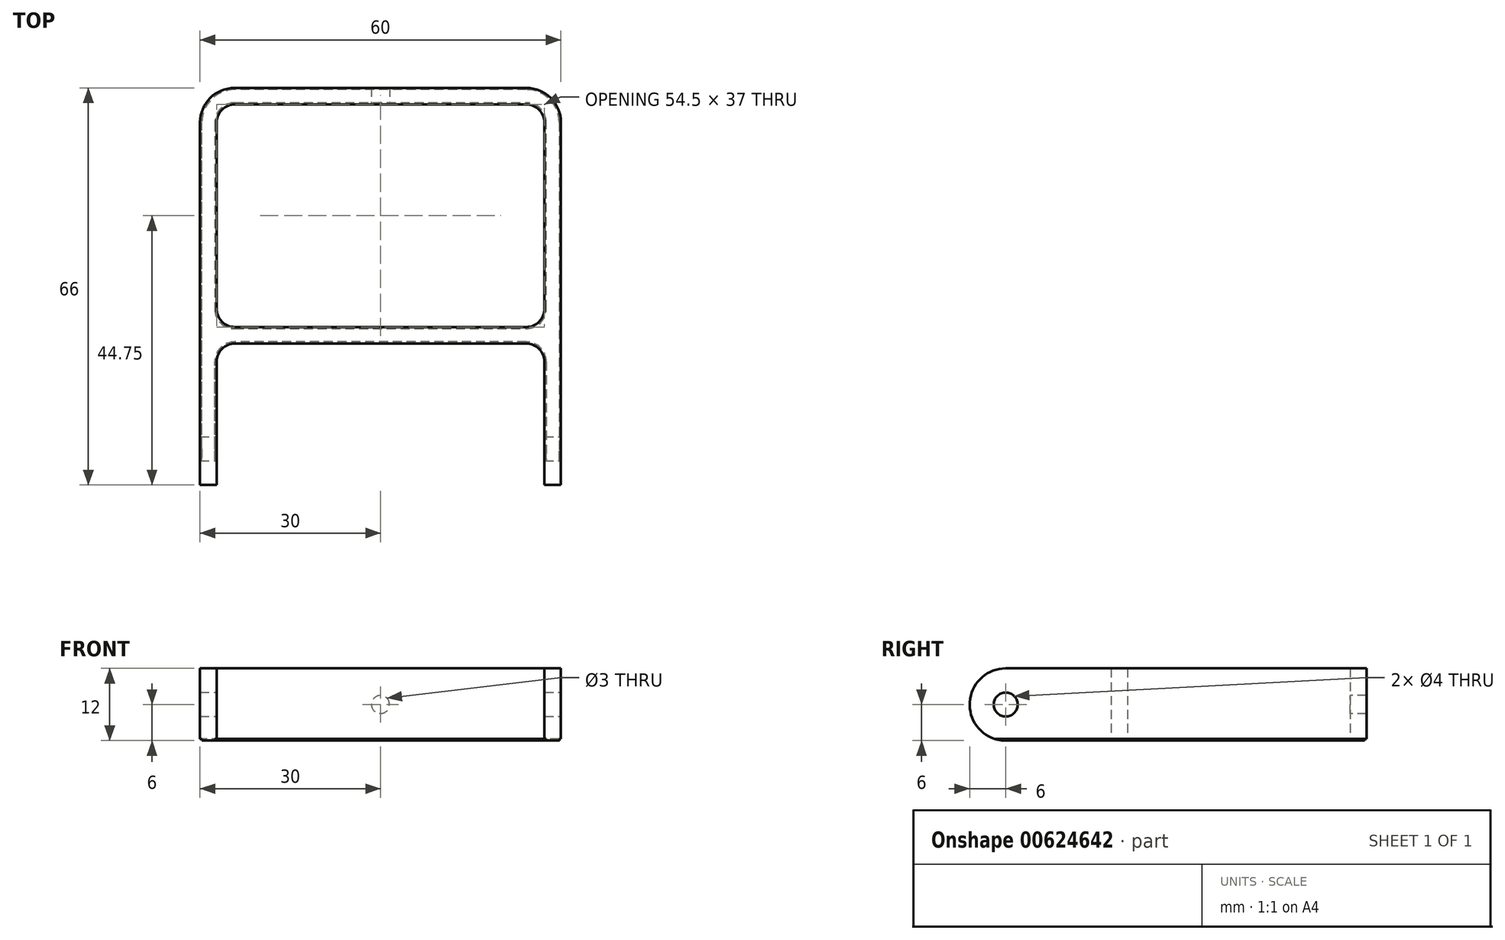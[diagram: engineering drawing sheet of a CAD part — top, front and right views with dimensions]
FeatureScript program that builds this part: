
annotation { "Feature Type Name" : "Feature", "Feature Type Description" : "" }
export const myFeature = defineFeature(function(context is Context, id is Id, definition is map)
    precondition{}
    {
        {
            var Q0;
            Q0=qCreatedBy(makeId("Top.planeOp"),FACE);
            var sketch = newSketch(context, id + "F0", { "sketchPlane" : qUnion([Q0])});
            skLineSegment(sketch, "E0", {"start": v(0, 0) * mm, "end": v(0, 63.25) * mm, "construction": true});
            skLineSegment(sketch, "E1", {"start": v(-27.25, 63.25) * mm, "end": v(27.25, 63.25) * mm});
            skLineSegment(sketch, "E2", {"start": v(27.25, 0) * mm, "end": v(30, 0) * mm});
            skLineSegment(sketch, "E3", {"start": v(30, 0) * mm, "end": v(30, 66) * mm});
            skLineSegment(sketch, "E4", {"start": v(30, 66) * mm, "end": v(-30, 66) * mm});
            skLineSegment(sketch, "E5", {"start": v(-30, 66) * mm, "end": v(-30, 0) * mm});
            skLineSegment(sketch, "E6", {"start": v(-30, 0) * mm, "end": v(-27.25, 0) * mm});
            skLineSegment(sketch, "E7", {"start": v(-27.25, 63.25) * mm, "end": v(-27.25, 26.25) * mm});
            skLineSegment(sketch, "E8", {"start": v(-27.25, 26.25) * mm, "end": v(27.25, 26.25) * mm});
            skLineSegment(sketch, "E9", {"start": v(27.25, 26.25) * mm, "end": v(27.25, 63.25) * mm});
            skLineSegment(sketch, "E10", {"start": v(27.25, 0) * mm, "end": v(27.25, 23.5) * mm});
            skLineSegment(sketch, "E11", {"start": v(27.25, 23.5) * mm, "end": v(-27.25, 23.5) * mm});
            skLineSegment(sketch, "E12", {"start": v(-27.25, 23.5) * mm, "end": v(-27.25, 0) * mm});
            skLineSegment(sketch, "E13", {"start": v(-27.25, 26.25) * mm, "end": v(-27.25, 23.5) * mm, "construction": true});
            skLineSegment(sketch, "E14", {"start": v(-27.25, 26.25) * mm, "end": v(-30, 26.25) * mm, "construction": true});
            skLineSegment(sketch, "E15", {"start": v(-27.25, 63.25) * mm, "end": v(-27.25, 66) * mm, "construction": true});
            skSolve(sketch);
        }
        {
            var Q0;
            Q0=qSketchRegion(id+"F0",true);
            extrude(context, id + "F1", {"entities" : qUnion([Q0]), "depth" : 12 * mm});
        }
        {
            var Q0;
            Q0=makeQuery(id+"F1.opExtrude","CAP_EDGE",EDGE,{"disambiguationData":[OSD([sQuery(id+"F0.wireOp",EDGE,"E6")])],"isStart":false});
            var Q1;
            Q1=makeQuery(id+"F1.opExtrude","CAP_EDGE",EDGE,{"disambiguationData":[OSD([sQuery(id+"F0.wireOp",EDGE,"E6")])],"isStart":true});
            var Q2;
            Q2=makeQuery(id+"F1.opExtrude","CAP_EDGE",EDGE,{"disambiguationData":[OSD([sQuery(id+"F0.wireOp",EDGE,"E2")])],"isStart":false});
            var Q3;
            Q3=makeQuery(id+"F1.opExtrude","CAP_EDGE",EDGE,{"disambiguationData":[OSD([sQuery(id+"F0.wireOp",EDGE,"E2")])],"isStart":true});
            fillet(context, id + "F2", {"entities" : qUnion([Q0, Q1, Q2, Q3]), "radius" : 6 * mm, "tangentPropagation" : true, "allowEdgeOverflow" : false});
        }
        {
            var Q0;
            Q0=makeQuery(id+"F1.opExtrude","SWEPT_FACE",FACE,{"disambiguationData":[OSD([sQuery(id+"F0.wireOp",EDGE,"E3")])]});
            var sketch = newSketch(context, id + "F3", { "sketchPlane" : qUnion([Q0])});
            skCircle(sketch, "E16", {"center": v(6, 6) * mm, "radius": 2 * mm});
            skSolve(sketch);
        }
        {
            var Q0;
            Q0=qSketchRegion(id+"F3",true);
            extrude(context, id + "F4", {"entities" : qUnion([Q0]), "operationType" : NewBodyOperationType.REMOVE, "endBound" : BoundingType.THROUGH_ALL, "oppositeDirection" : true, "depth" : 25 * mm});
        }
        {
            var Q0;
            Q0=makeQuery(id+"F1.opExtrude","SWEPT_FACE",FACE,{"disambiguationData":[OSD([sQuery(id+"F0.wireOp",EDGE,"E1")])]});
            var sketch = newSketch(context, id + "F5", { "sketchPlane" : qUnion([Q0])});
            skLineSegment(sketch, "E17", {"start": v(0, 12) * mm, "end": v(0, 0) * mm, "construction": true});
            skCircle(sketch, "E18", {"center": v(0, 6) * mm, "radius": 1.5 * mm});
            skSolve(sketch);
        }
        {
            var Q0;
            Q0=qSketchRegion(id+"F5",true);
            var Q1;
            Q1=makeQuery(id+"F1.opExtrude","SWEPT_FACE",FACE,{"disambiguationData":[OSD([sQuery(id+"F0.wireOp",EDGE,"E4")])]});
            extrude(context, id + "F6", {"entities" : qUnion([Q0]), "operationType" : NewBodyOperationType.REMOVE, "endBound" : BoundingType.UP_TO_SURFACE, "oppositeDirection" : true, "endBoundEntityFace" : qUnion([Q1]), "depth" : 25 * mm});
        }
        {
            var Q0;
            Q0=makeQuery(id+"F1.opExtrude","SWEPT_EDGE",EDGE,{"disambiguationData":[OSD([sQuery(id+"F0.wireOp",EDGE,"E1"),sQuery(id+"F0.wireOp",EDGE,"E7")])]});
            var Q1;
            Q1=makeQuery(id+"F1.opExtrude","SWEPT_EDGE",EDGE,{"disambiguationData":[OSD([sQuery(id+"F0.wireOp",EDGE,"E11"),sQuery(id+"F0.wireOp",EDGE,"E12")])]});
            var Q2;
            Q2=makeQuery(id+"F1.opExtrude","SWEPT_EDGE",EDGE,{"disambiguationData":[OSD([sQuery(id+"F0.wireOp",EDGE,"E7"),sQuery(id+"F0.wireOp",EDGE,"E8")])]});
            var Q3;
            Q3=makeQuery(id+"F1.opExtrude","SWEPT_EDGE",EDGE,{"disambiguationData":[OSD([sQuery(id+"F0.wireOp",EDGE,"E1"),sQuery(id+"F0.wireOp",EDGE,"E9")])]});
            var Q4;
            Q4=makeQuery(id+"F1.opExtrude","SWEPT_EDGE",EDGE,{"disambiguationData":[OSD([sQuery(id+"F0.wireOp",EDGE,"E10"),sQuery(id+"F0.wireOp",EDGE,"E11")])]});
            var Q5;
            Q5=makeQuery(id+"F1.opExtrude","SWEPT_EDGE",EDGE,{"disambiguationData":[OSD([sQuery(id+"F0.wireOp",EDGE,"E8"),sQuery(id+"F0.wireOp",EDGE,"E9")])]});
            fillet(context, id + "F7", {"entities" : qUnion([Q0, Q1, Q2, Q3, Q4, Q5]), "radius" : 3 * mm, "tangentPropagation" : true, "allowEdgeOverflow" : false});
        }
        {
            var Q0;
            Q0=makeQuery(id+"F1.opExtrude","SWEPT_EDGE",EDGE,{"disambiguationData":[OSD([sQuery(id+"F0.wireOp",EDGE,"E4"),sQuery(id+"F0.wireOp",EDGE,"E5")])]});
            var Q1;
            Q1=makeQuery(id+"F1.opExtrude","SWEPT_EDGE",EDGE,{"disambiguationData":[OSD([sQuery(id+"F0.wireOp",EDGE,"E3"),sQuery(id+"F0.wireOp",EDGE,"E4")])]});
            fillet(context, id + "F8", {"entities" : qUnion([Q0, Q1]), "radius" : 5.75 * mm, "tangentPropagation" : true, "allowEdgeOverflow" : false});
        }
        {
            var Q0;
            Q0=makeQuery(id+"F1.opExtrude","CAP_FACE",FACE,{"disambiguationData":[OSD([sQuery(id+"F0.wireOp",EDGE,"E1"),sQuery(id+"F0.wireOp",EDGE,"E2"),sQuery(id+"F0.wireOp",EDGE,"E3"),sQuery(id+"F0.wireOp",EDGE,"E4"),sQuery(id+"F0.wireOp",EDGE,"E5"),sQuery(id+"F0.wireOp",EDGE,"E6"),sQuery(id+"F0.wireOp",EDGE,"E7"),sQuery(id+"F0.wireOp",EDGE,"E8"),sQuery(id+"F0.wireOp",EDGE,"E9"),sQuery(id+"F0.wireOp",EDGE,"E10"),sQuery(id+"F0.wireOp",EDGE,"E11"),sQuery(id+"F0.wireOp",EDGE,"E12")])],"isStart":true});
            var sketch = newSketch(context, id + "F9", { "sketchPlane" : qUnion([Q0])});
            skLineSegment(sketch, "E19.0", {"start": v(30, -6) * mm, "end": v(30, -60.25) * mm});
            skArc(sketch, "E19.1", {"start": v(24.25, -66) * mm, "mid": v(28.32, -64.32) * mm, "end": v(30, -60.25) * mm});
            skLineSegment(sketch, "E19.3", {"start": v(24.25, -66) * mm, "end": v(-24.25, -66) * mm});
            skArc(sketch, "E19.8", {"start": v(27.25, -20.5) * mm, "mid": v(26.37, -22.62) * mm, "end": v(24.25, -23.5) * mm});
            skLineSegment(sketch, "E19.9", {"start": v(27.25, -6) * mm, "end": v(27.25, -20.5) * mm});
            skLineSegment(sketch, "E19.10", {"start": v(24.25, -23.5) * mm, "end": v(-24.25, -23.5) * mm});
            skArc(sketch, "E19.11", {"start": v(-24.25, -23.5) * mm, "mid": v(-26.37, -22.62) * mm, "end": v(-27.25, -20.5) * mm});
            skLineSegment(sketch, "E19.12", {"start": v(-27.25, -20.5) * mm, "end": v(-27.25, -6) * mm});
            skLineSegment(sketch, "E19.13", {"start": v(-30, -60.25) * mm, "end": v(-30, -6) * mm});
            skArc(sketch, "E19.17", {"start": v(-30, -60.25) * mm, "mid": v(-28.32, -64.32) * mm, "end": v(-24.25, -66) * mm});
            skLineSegment(sketch, "E20.0", {"start": v(27.25, -6) * mm, "end": v(27.25, 0) * mm});
            skLineSegment(sketch, "E21.0", {"start": v(30, -6) * mm, "end": v(30, 0) * mm});
            skLineSegment(sketch, "E22.0", {"start": v(-30, 0) * mm, "end": v(-30, -6) * mm});
            skLineSegment(sketch, "E22.1", {"start": v(-27.25, 0) * mm, "end": v(-27.25, -6) * mm});
            skLineSegment(sketch, "E23.0", {"start": v(27.55, -6) * mm, "end": v(27.55, 0) * mm});
            skLineSegment(sketch, "E23.1", {"start": v(27.55, -6) * mm, "end": v(27.55, -20.5) * mm});
            skArc(sketch, "E23.2", {"start": v(27.55, -20.5) * mm, "mid": v(26.58, -22.83) * mm, "end": v(24.25, -23.8) * mm});
            skLineSegment(sketch, "E23.3", {"start": v(24.25, -23.8) * mm, "end": v(-24.25, -23.8) * mm});
            skArc(sketch, "E23.4", {"start": v(-24.25, -23.8) * mm, "mid": v(-26.58, -22.83) * mm, "end": v(-27.55, -20.5) * mm});
            skLineSegment(sketch, "E23.5", {"start": v(-27.55, -20.5) * mm, "end": v(-27.55, -6) * mm});
            skLineSegment(sketch, "E23.6", {"start": v(-27.55, 0) * mm, "end": v(-27.55, -6) * mm});
            skLineSegment(sketch, "E24", {"start": v(-27.55, 0) * mm, "end": v(-27.25, 0) * mm});
            skLineSegment(sketch, "E25", {"start": v(27.55, 0) * mm, "end": v(27.25, 0) * mm});
            skLineSegment(sketch, "E26.0", {"start": v(29.7, -6) * mm, "end": v(29.7, 0) * mm});
            skLineSegment(sketch, "E26.1", {"start": v(29.7, -6) * mm, "end": v(29.7, -60.25) * mm});
            skArc(sketch, "E26.2", {"start": v(24.25, -65.7) * mm, "mid": v(28.1, -64.1) * mm, "end": v(29.7, -60.25) * mm});
            skLineSegment(sketch, "E26.3", {"start": v(24.25, -65.7) * mm, "end": v(-24.25, -65.7) * mm});
            skArc(sketch, "E26.4", {"start": v(-29.7, -60.25) * mm, "mid": v(-28.1, -64.1) * mm, "end": v(-24.25, -65.7) * mm});
            skLineSegment(sketch, "E26.5", {"start": v(-29.7, -60.25) * mm, "end": v(-29.7, -6) * mm});
            skLineSegment(sketch, "E26.6", {"start": v(-29.7, 0) * mm, "end": v(-29.7, -6) * mm});
            skLineSegment(sketch, "E27", {"start": v(30, 0) * mm, "end": v(29.7, 0) * mm});
            skLineSegment(sketch, "E28", {"start": v(-29.7, 0) * mm, "end": v(-30, 0) * mm});
            skSolve(sketch);
        }
        {
            var Q0;
            Q0=qSketchRegion(id+"F9",true);
            extrude(context, id + "F10", {"entities" : qUnion([Q0]), "operationType" : NewBodyOperationType.REMOVE, "oppositeDirection" : true, "depth" : 0.3 * mm});
        }
        {
            var Q0;
            Q0=makeQuery(id+"F1.opExtrude","CAP_FACE",FACE,{"disambiguationData":[OSD([sQuery(id+"F0.wireOp",EDGE,"E1"),sQuery(id+"F0.wireOp",EDGE,"E2"),sQuery(id+"F0.wireOp",EDGE,"E3"),sQuery(id+"F0.wireOp",EDGE,"E4"),sQuery(id+"F0.wireOp",EDGE,"E5"),sQuery(id+"F0.wireOp",EDGE,"E6"),sQuery(id+"F0.wireOp",EDGE,"E7"),sQuery(id+"F0.wireOp",EDGE,"E8"),sQuery(id+"F0.wireOp",EDGE,"E9"),sQuery(id+"F0.wireOp",EDGE,"E10"),sQuery(id+"F0.wireOp",EDGE,"E11"),sQuery(id+"F0.wireOp",EDGE,"E12")])],"isStart":true});
            var sketch = newSketch(context, id + "F11", { "sketchPlane" : qUnion([Q0])});
            skArc(sketch, "E29.0", {"start": v(24.25, -26.25) * mm, "mid": v(26.37, -27.13) * mm, "end": v(27.25, -29.25) * mm});
            skLineSegment(sketch, "E29.1", {"start": v(27.25, -29.25) * mm, "end": v(27.25, -60.25) * mm});
            skArc(sketch, "E29.2", {"start": v(27.25, -60.25) * mm, "mid": v(26.37, -62.37) * mm, "end": v(24.25, -63.25) * mm});
            skLineSegment(sketch, "E29.3", {"start": v(-24.25, -63.25) * mm, "end": v(24.25, -63.25) * mm});
            skArc(sketch, "E29.4", {"start": v(-24.25, -63.25) * mm, "mid": v(-26.37, -62.37) * mm, "end": v(-27.25, -60.25) * mm});
            skLineSegment(sketch, "E29.5", {"start": v(-27.25, -60.25) * mm, "end": v(-27.25, -29.25) * mm});
            skArc(sketch, "E29.6", {"start": v(-27.25, -29.25) * mm, "mid": v(-26.37, -27.13) * mm, "end": v(-24.25, -26.25) * mm});
            skLineSegment(sketch, "E29.7", {"start": v(-24.25, -26.25) * mm, "end": v(24.25, -26.25) * mm});
            skArc(sketch, "E30.0", {"start": v(-27.55, -29.25) * mm, "mid": v(-26.58, -26.92) * mm, "end": v(-24.25, -25.95) * mm});
            skLineSegment(sketch, "E30.1", {"start": v(-27.55, -60.25) * mm, "end": v(-27.55, -29.25) * mm});
            skArc(sketch, "E30.2", {"start": v(-24.25, -63.55) * mm, "mid": v(-26.58, -62.58) * mm, "end": v(-27.55, -60.25) * mm});
            skLineSegment(sketch, "E30.3", {"start": v(-24.25, -63.55) * mm, "end": v(24.25, -63.55) * mm});
            skArc(sketch, "E30.4", {"start": v(27.55, -60.25) * mm, "mid": v(26.58, -62.58) * mm, "end": v(24.25, -63.55) * mm});
            skLineSegment(sketch, "E30.5", {"start": v(-24.25, -25.95) * mm, "end": v(24.25, -25.95) * mm});
            skLineSegment(sketch, "E30.6", {"start": v(27.55, -29.25) * mm, "end": v(27.55, -60.25) * mm});
            skArc(sketch, "E30.7", {"start": v(24.25, -25.95) * mm, "mid": v(26.58, -26.92) * mm, "end": v(27.55, -29.25) * mm});
            skSolve(sketch);
        }
        {
            var Q0;
            Q0=qSketchRegion(id+"F11",true);
            extrude(context, id + "F12", {"entities" : qUnion([Q0]), "operationType" : NewBodyOperationType.REMOVE, "oppositeDirection" : true, "depth" : 0.3 * mm});
        }
    });
